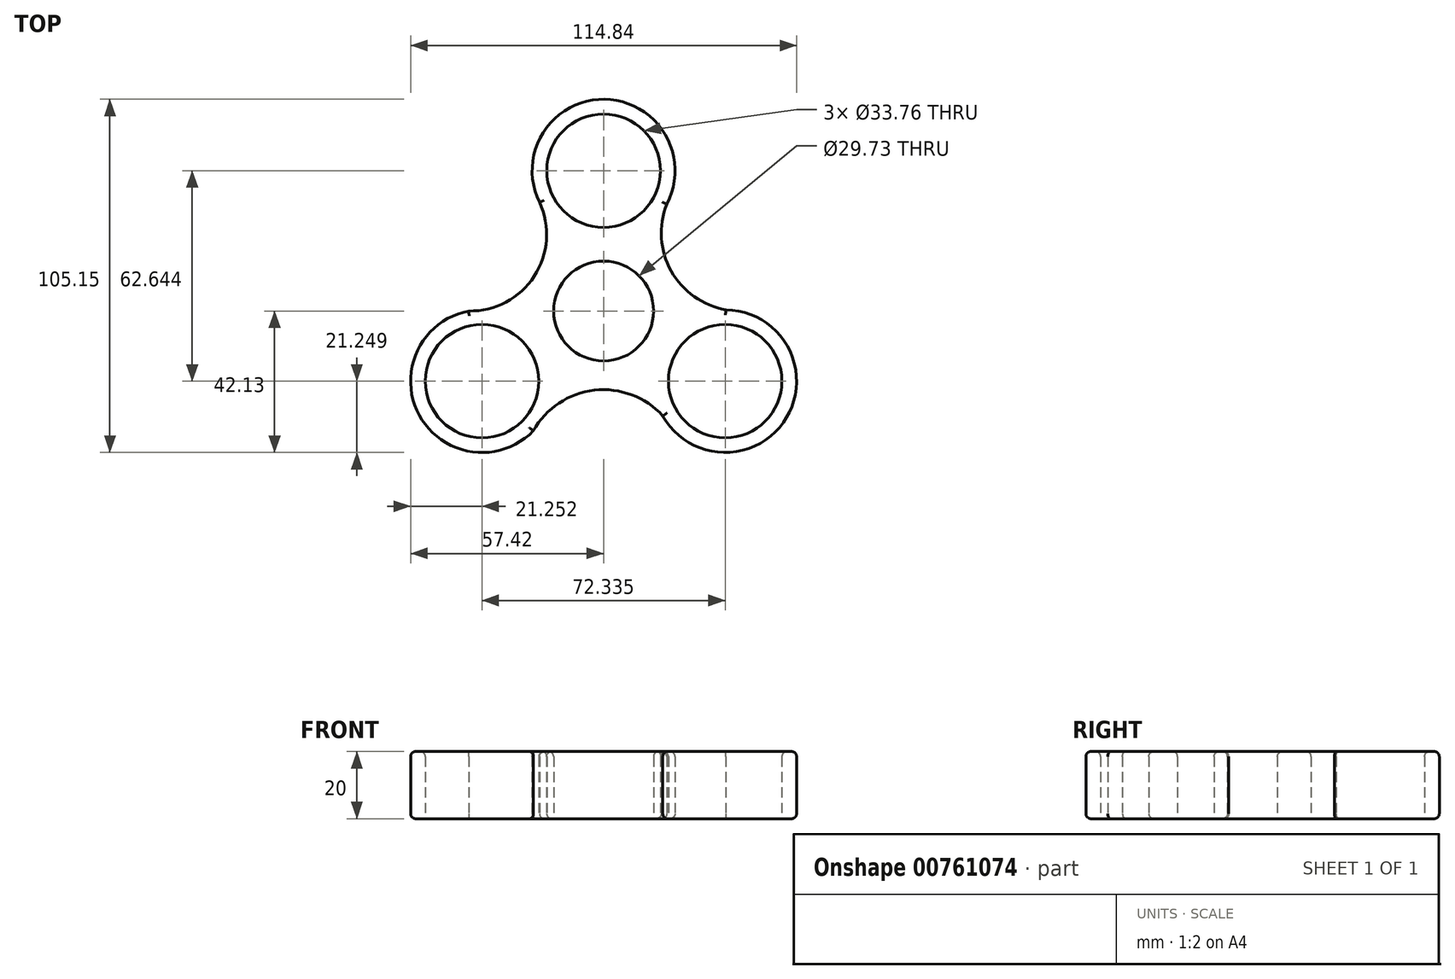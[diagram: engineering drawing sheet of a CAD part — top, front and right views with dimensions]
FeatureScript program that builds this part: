
annotation { "Feature Type Name" : "Feature", "Feature Type Description" : "" }
export const myFeature = defineFeature(function(context is Context, id is Id, definition is map)
    precondition{}
    {
        {
            var Q0;
            Q0=qCreatedBy(makeId("Top.planeOp"),FACE);
            var sketch = newSketch(context, id + "F0", { "sketchPlane" : qUnion([Q0])});
            skCircle(sketch, "E0", {"center": v(0, 0) * mm, "radius": 14.86 * mm});
            skCircle(sketch, "E1", {"center": v(0, 41.76) * mm, "radius": 16.88 * mm});
            skArc(sketch, "E2", {"start": v(18.77, 31.8) * mm, "mid": v(0.3, 63.01) * mm, "end": v(-19.04, 32.33) * mm});
            skCircle(sketch, "E3.1.0", {"center": v(-36.17, -20.88) * mm, "radius": 16.88 * mm});
            skArc(sketch, "E3.1.1", {"start": v(-35.65, 0.36) * mm, "mid": v(-54.55, -31.55) * mm, "end": v(-17.47, -30.98) * mm});
            skCircle(sketch, "E3.2.0", {"center": v(36.17, -20.88) * mm, "radius": 16.88 * mm});
            skArc(sketch, "E3.2.1", {"start": v(17.61, -31.24) * mm, "mid": v(54.44, -31.73) * mm, "end": v(36.39, 0.37) * mm});
            skArc(sketch, "E4", {"start": v(18.77, 31.8) * mm, "mid": v(20.11, 11.9) * mm, "end": v(36.39, 0.37) * mm});
            skArc(sketch, "E5", {"start": v(17.61, -31.24) * mm, "mid": v(-2.76, -23.58) * mm, "end": v(-20.88, -35.64) * mm});
            skArc(sketch, "E6", {"start": v(-40.12, 0) * mm, "mid": v(-20.64, 10.33) * mm, "end": v(-19.04, 32.33) * mm});
            skSolve(sketch);
        }
        {
            var Q0;
            Q0=makeQuery(id+"F0.imprint","IMPRINT",FACE,{"disambiguationData":[TD([[makeQuery(id+"F0.imprint","IMPRINT",EDGE,{"derivedFrom":sQuery(id+"F0.wireOp",EDGE,"E0")}),-1.0]])]});
            extrude(context, id + "F1", {"entities" : qUnion([Q0]), "depth" : 20 * mm, "offsetDistance" : 25 * mm});
        }
        {
            var Q0;
            Q0=makeQuery(id+"F1.opExtrude","CAP_EDGE",EDGE,{"disambiguationData":[OSD([sQuery(id+"F0.wireOp",EDGE,"E3.1.1")])],"isStart":false});
            var Q1;
            Q1=makeQuery(id+"F1.opExtrude","CAP_FACE",FACE,{"disambiguationData":[OSD([sQuery(id+"F0.wireOp",EDGE,"E0"),sQuery(id+"F0.wireOp",EDGE,"E1"),sQuery(id+"F0.wireOp",EDGE,"E2"),sQuery(id+"F0.wireOp",EDGE,"E3.1.0"),sQuery(id+"F0.wireOp",EDGE,"E3.1.1"),sQuery(id+"F0.wireOp",EDGE,"E3.2.0"),sQuery(id+"F0.wireOp",EDGE,"E3.2.1"),sQuery(id+"F0.wireOp",EDGE,"E4"),sQuery(id+"F0.wireOp",EDGE,"E5"),sQuery(id+"F0.wireOp",EDGE,"E6")])],"isStart":false});
            var Q2;
            Q2=makeQuery(id+"F1.opExtrude","CAP_EDGE",EDGE,{"disambiguationData":[OSD([sQuery(id+"F0.wireOp",EDGE,"E2")])],"isStart":false});
            var Q3;
            Q3=makeQuery(id+"F1.opExtrude","CAP_EDGE",EDGE,{"disambiguationData":[OSD([sQuery(id+"F0.wireOp",EDGE,"E4")])],"isStart":false});
            fillet(context, id + "F2", {"entities" : qUnion([Q0, Q1, Q2, Q3]), "radius" : 1.5 * mm, "tangentPropagation" : true, "allowEdgeOverflow" : false});
        }
        {
            var Q0;
            Q0=makeQuery(id+"F1.opExtrude","CAP_EDGE",EDGE,{"disambiguationData":[OSD([sQuery(id+"F0.wireOp",EDGE,"E5")])],"isStart":true});
            var Q1;
            Q1=makeQuery(id+"F1.opExtrude","CAP_EDGE",EDGE,{"disambiguationData":[OSD([sQuery(id+"F0.wireOp",EDGE,"E3.2.1")])],"isStart":true});
            var Q2;
            Q2=makeQuery(id+"F1.opExtrude","CAP_EDGE",EDGE,{"disambiguationData":[OSD([sQuery(id+"F0.wireOp",EDGE,"E4")])],"isStart":true});
            var Q3;
            Q3=makeQuery(id+"F1.opExtrude","CAP_EDGE",EDGE,{"disambiguationData":[OSD([sQuery(id+"F0.wireOp",EDGE,"E2")])],"isStart":true});
            var Q4;
            Q4=makeQuery(id+"F1.opExtrude","CAP_EDGE",EDGE,{"disambiguationData":[OSD([sQuery(id+"F0.wireOp",EDGE,"E6")])],"isStart":true});
            var Q5;
            Q5=makeQuery(id+"F1.opExtrude","CAP_EDGE",EDGE,{"disambiguationData":[OSD([sQuery(id+"F0.wireOp",EDGE,"E3.1.1")])],"isStart":true});
            fillet(context, id + "F3", {"entities" : qUnion([Q0, Q1, Q2, Q3, Q4, Q5]), "radius" : 1.5 * mm, "tangentPropagation" : true, "allowEdgeOverflow" : false});
        }
    });
